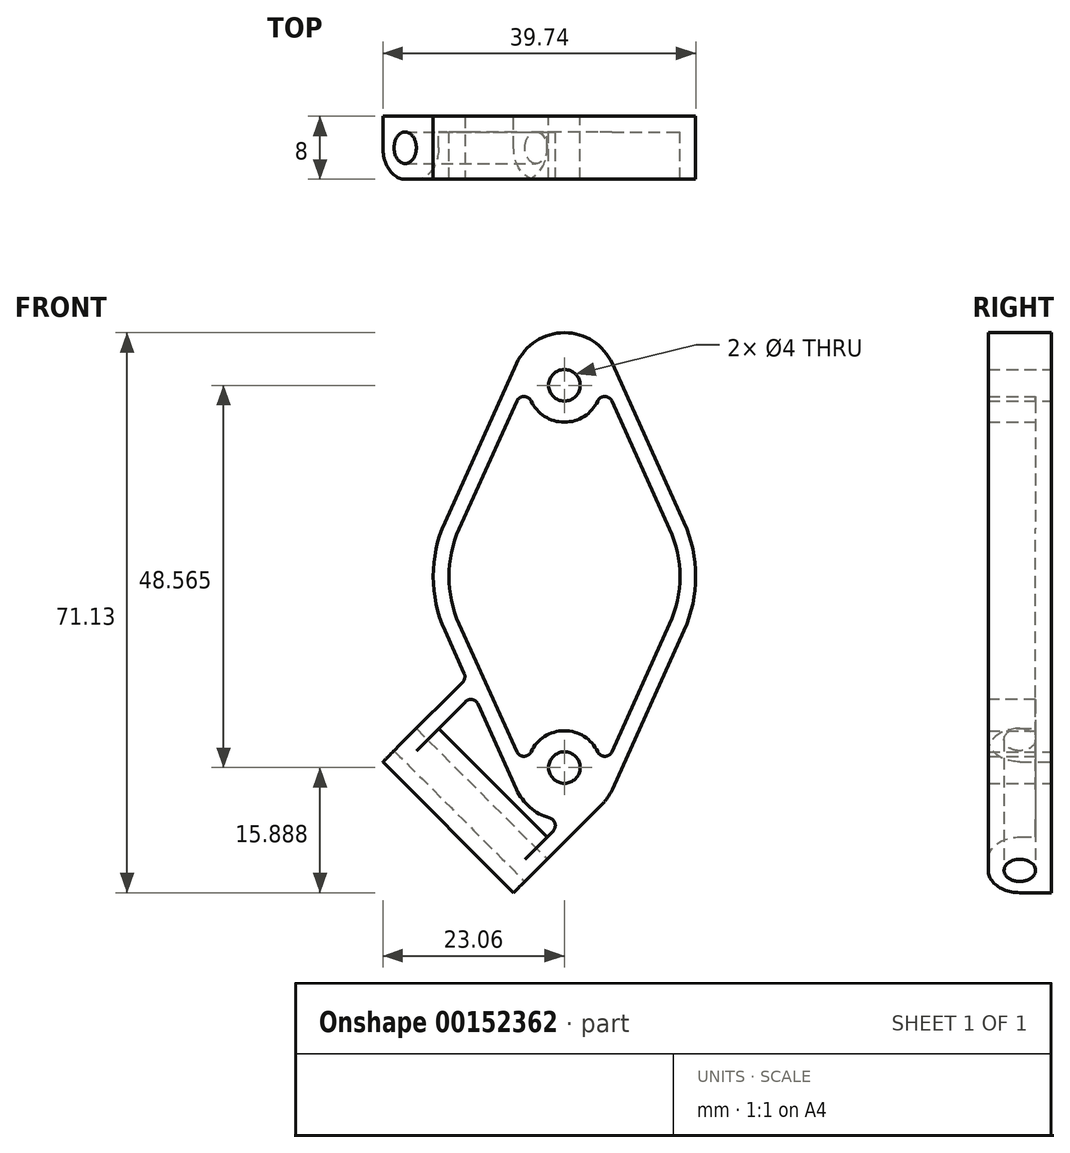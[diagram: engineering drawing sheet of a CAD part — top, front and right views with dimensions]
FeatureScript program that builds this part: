
annotation { "Feature Type Name" : "Feature", "Feature Type Description" : "" }
export const myFeature = defineFeature(function(context is Context, id is Id, definition is map)
    precondition{}
    {
        {
            var Q0;
            Q0=qCreatedBy(makeId("Front.planeOp"),FACE);
            var sketch = newSketch(context, id + "F0", { "sketchPlane" : qUnion([Q0])});
            skArc(sketch, "E0", {"start": v(6.09, 27.03) * mm, "mid": v(0, 30.96) * mm, "end": v(-6.09, 27.03) * mm});
            skArc(sketch, "E1.MirrorC", {"start": v(6.09, -27.03) * mm, "mid": v(0, -30.96) * mm, "end": v(-6.09, -27.03) * mm});
            skArc(sketch, "E2", {"start": v(-15.2, 6.86) * mm, "mid": v(-16.68, 0) * mm, "end": v(-15.2, -6.86) * mm});
            skLineSegment(sketch, "E3", {"start": v(-6.09, 27.03) * mm, "end": v(-15.2, 6.86) * mm});
            skLineSegment(sketch, "E4.MirrorCS", {"start": v(-6.09, -27.03) * mm, "end": v(-15.2, -6.86) * mm});
            skLineSegment(sketch, "E5.MirrorCS", {"start": v(6.09, 27.03) * mm, "end": v(15.2, 6.86) * mm});
            skLineSegment(sketch, "E6.MirrorCS", {"start": v(6.09, -27.03) * mm, "end": v(15.2, -6.86) * mm});
            skArc(sketch, "E7.trimOffspring", {"start": v(15.2, -6.86) * mm, "mid": v(16.68, 0) * mm, "end": v(15.2, 6.86) * mm});
            skCircle(sketch, "E8", {"center": v(0, 24.28) * mm, "radius": 2 * mm});
            skCircle(sketch, "E9.MirrorC", {"center": v(0, -24.28) * mm, "radius": 2 * mm});
            skLineSegment(sketch, "E10.1", {"start": v(-6.05, 22.27) * mm, "end": v(-13.37, 6.04) * mm});
            skLineSegment(sketch, "E10.2", {"start": v(6.05, 22.27) * mm, "end": v(13.37, 6.04) * mm});
            skArc(sketch, "E10.3", {"start": v(-13.37, 6.04) * mm, "mid": v(-14.68, 0) * mm, "end": v(-13.37, -6.04) * mm});
            skArc(sketch, "E10.4", {"start": v(13.37, -6.04) * mm, "mid": v(14.68, 0) * mm, "end": v(13.37, 6.04) * mm});
            skLineSegment(sketch, "E10.5", {"start": v(6.05, -22.27) * mm, "end": v(13.37, -6.04) * mm});
            skLineSegment(sketch, "E10.7", {"start": v(-6.05, -22.27) * mm, "end": v(-13.37, -6.04) * mm});
            skArc(sketch, "E11", {"start": v(-4.23, 22.28) * mm, "mid": v(0, 19.6) * mm, "end": v(4.23, 22.28) * mm});
            skArc(sketch, "E12", {"start": v(4.23, -22.28) * mm, "mid": v(0, -19.6) * mm, "end": v(-4.23, -22.28) * mm});
            skPoint(sketch, "E13.visualSharp", {"position": v(-4.27, 26.2) * mm});
            skArc(sketch, "E13.filletArc", {"start": v(-4.23, 22.28) * mm, "mid": v(-5.14, 22.85) * mm, "end": v(-6.05, 22.27) * mm});
            skPoint(sketch, "E14.visualSharp", {"position": v(4.27, 26.2) * mm});
            skArc(sketch, "E14.filletArc", {"start": v(6.05, 22.27) * mm, "mid": v(5.14, 22.85) * mm, "end": v(4.23, 22.28) * mm});
            skPoint(sketch, "E15.visualSharp", {"position": v(4.27, -26.2) * mm});
            skArc(sketch, "E15.filletArc", {"start": v(4.23, -22.28) * mm, "mid": v(5.14, -22.85) * mm, "end": v(6.05, -22.27) * mm});
            skPoint(sketch, "E16.visualSharp", {"position": v(-4.27, -26.2) * mm});
            skArc(sketch, "E16.filletArc", {"start": v(-6.05, -22.27) * mm, "mid": v(-5.14, -22.85) * mm, "end": v(-4.23, -22.28) * mm});
            skLineSegment(sketch, "E17", {"start": v(58.04, 58.04) * mm, "end": v(-58.68, -58.68) * mm, "construction": true});
            skLineSegment(sketch, "E18", {"start": v(4.72, -29) * mm, "end": v(-6.44, -40.17) * mm});
            skLineSegment(sketch, "E19", {"start": v(-6.44, -40.17) * mm, "end": v(-23.06, -23.55) * mm});
            skLineSegment(sketch, "E20", {"start": v(-23.06, -23.55) * mm, "end": v(-12.45, -12.95) * mm});
            skLineSegment(sketch, "E21", {"start": v(-11.57, -14.9) * mm, "end": v(-15.99, -19.3) * mm});
            skLineSegment(sketch, "E22", {"start": v(-15.99, -19.3) * mm, "end": v(-2.2, -33.1) * mm});
            skLineSegment(sketch, "E23", {"start": v(-2.2, -33.1) * mm, "end": v(-0.06, -30.96) * mm});
            skSolve(sketch);
        }
        {
            var Q0;
            Q0=makeQuery(id+"F0.imprint","IMPRINT",FACE,{"disambiguationData":[TD([[makeQuery(id+"F0.imprint","IMPRINT",EDGE,{"derivedFrom":sQuery(id+"F0.wireOp",EDGE,"E0")}),1.0]])]});
            var Q1;
            {var subQ0=sQuery(id+"F0.wireOp",EDGE,"E18");Q1=makeQuery(id+"F0.imprint","IMPRINT",FACE,{"disambiguationData":[TD([[makeQuery(id+"F0.imprint","IMPRINT",EDGE,{"derivedFrom":subQ0}),-1.0]])]});}
            extrude(context, id + "F1", {"entities" : qUnion([Q0, Q1]), "depth" : 8 * mm});
        }
        {
            var Q0;
            Q0=makeQuery(id+"F0.imprint","IMPRINT",FACE,{"disambiguationData":[TD([[makeQuery(id+"F0.imprint","IMPRINT",EDGE,{"derivedFrom":sQuery(id+"F0.wireOp",EDGE,"E10.1")}),1.0]])]});
            var Q1;
            {var subQ4=sQuery(id+"F0.wireOp",EDGE,"E21");Q1=makeQuery(id+"F0.imprint","IMPRINT",FACE,{"disambiguationData":[TD([[makeQuery(id+"F0.imprint","IMPRINT",EDGE,{"derivedFrom":subQ4}),1.0]])]});}
            extrude(context, id + "F2", {"entities" : qUnion([Q0, Q1]), "operationType" : NewBodyOperationType.ADD, "depth" : 2 * mm});
        }
        {
            var Q0;
            Q0=makeQuery(id+"F1.opExtrude","SWEPT_EDGE",EDGE,{"disambiguationData":[OSD([sQuery(id+"F0.wireOp",EDGE,"E4.MirrorCS"),sQuery(id+"F0.wireOp",EDGE,"E20")])]});
            var Q1;
            Q1=makeQuery(id+"F1.opExtrude","SWEPT_EDGE",EDGE,{"disambiguationData":[OSD([sQuery(id+"F0.wireOp",EDGE,"E4.MirrorCS"),sQuery(id+"F0.wireOp",EDGE,"E21")])]});
            var Q2;
            Q2=makeQuery(id+"F1.opExtrude","SWEPT_EDGE",EDGE,{"disambiguationData":[OSD([sQuery(id+"F0.wireOp",EDGE,"E1.MirrorC"),sQuery(id+"F0.wireOp",EDGE,"E23")])]});
            fillet(context, id + "F3", {"entities" : qUnion([Q0, Q1, Q2]), "radius" : 1 * mm, "tangentPropagation" : true, "allowEdgeOverflow" : false});
        }
        {
            var Q0;
            Q0=makeQuery(id+"F1.opExtrude","SWEPT_FACE",FACE,{"disambiguationData":[OSD([sQuery(id+"F0.wireOp",EDGE,"E18")])]});
            var sketch = newSketch(context, id + "F4", { "sketchPlane" : qUnion([Q0])});
            skPoint(sketch, "E24", {"position": v(-4, -28.96) * mm});
            skLineSegment(sketch, "E25", {"start": v(-8, -32.96) * mm, "end": v(-4, -28.96) * mm, "construction": true});
            skLineSegment(sketch, "E26", {"start": v(-4, -28.96) * mm, "end": v(0, -32.96) * mm, "construction": true});
            skSolve(sketch);
        }
        {
            var Q0;
            Q0=sQuery(id+"F4.wireOp",VERTEX,"E24");
            var Q1;
            Q1=makeQuery(id+"F1.opExtrude","SWEPT_BODY",BODY,{"disambiguationData":[OSD([sQuery(id+"F0.wireOp",EDGE,"E0"),sQuery(id+"F0.wireOp",EDGE,"E2"),sQuery(id+"F0.wireOp",EDGE,"E3"),sQuery(id+"F0.wireOp",EDGE,"E5.MirrorCS"),sQuery(id+"F0.wireOp",EDGE,"E7.trimOffspring"),sQuery(id+"F0.wireOp",EDGE,"S2IiUO7s-7rjS-UU1n-G3Er-isHJvikYOna3"),sQuery(id+"F0.wireOp",EDGE,"U4xu2M48-wPnJ-tMoa-V4Px-PJSouQ81H8F5"),sQuery(id+"F0.wireOp",EDGE,"HV652KFt-d8Xn-WSbo-tHCJ-cfUj0g3Xd7DK"),sQuery(id+"F0.wireOp",EDGE,"fO4OrWz9-9ff7-9GLH-ZSri-iVDJwJIuYxIB"),sQuery(id+"F0.wireOp",EDGE,"zmEnNPUg-k7De-l4Ih-Irfg-M27UcczaaJBl"),sQuery(id+"F0.wireOp",EDGE,"V3VQVJa9-jFdV-kq6X-8dhK-Xa6uhI9IwXRv"),sQuery(id+"F0.wireOp",EDGE,"W1IEodJy-6PRz-xiH1-2iNf-kAuRcIV7mYlj"),sQuery(id+"F0.wireOp",EDGE,"5ZKJKvnk-ET5z-qlB3-oLW5-LuLVHKlnV0HX"),sQuery(id+"F0.wireOp",EDGE,"Gk8awqwg-zgXA-VnUW-8MKI-QdblR6Wf13JX"),sQuery(id+"F0.wireOp",EDGE,"WIDdAYBM-okhh-eBsl-QBhJ-HuDdJqstO0Cl"),sQuery(id+"F0.wireOp",EDGE,"iXw4nrh7-EQqi-IiG2-VBaK-kNldmVsmUaTg"),sQuery(id+"F0.wireOp",EDGE,"03ff63bc-461f-42e4-a166-82e271801758"),sQuery(id+"F0.wireOp",EDGE,"5881da14-4dba-48e3-8e12-341ecdeeb7140.MirrorCS")])]});
            hole(context, id + "F5", {"style" : HoleStyle.SIMPLE, "endStyle" : HoleEndStyle.THROUGH, "standardTappedOrClearance" : lookupTablePath({ "standard" : "ISO", "size" : "4", "type" : "Drilled" }), "standardBlindInLast" : lookupTablePath({ "standard" : "ISO", "size" : "4", "type" : "Drilled" }), "holeDiameter" : 4 * mm, "locations" : qUnion([Q0]), "scope" : qUnion([Q1]), "isTappedThrough" : true});
        }
        {
            var Q0;
            Q0=makeQuery(id+"F1.opExtrude","CAP_EDGE",EDGE,{"disambiguationData":[OSD([sQuery(id+"F0.wireOp",EDGE,"E19")])],"isStart":false});
            var Q1;
            Q1=makeQuery(id+"F1.opExtrude","CAP_EDGE",EDGE,{"disambiguationData":[OSD([sQuery(id+"F0.wireOp",EDGE,"E22")])],"isStart":false});
            fillet(context, id + "F6", {"entities" : qUnion([Q0, Q1]), "radius" : (8 / 2) * mm, "tangentPropagation" : true, "allowEdgeOverflow" : false});
        }
    });
